# Revit family: Hager-Volta-IP30-Surface_mounted-leer-CH-de
name_source: partatom
category: Electrical Equipment
units: mm (PartAtom-declared; Revit-internal decimal feet)

## family parameters
Cut with Voids When Loaded = No
Host = Face
Panel Configuration = Two Columns, Circuits Across
Part Type = Panelboard
Room Calculation Point = No
Round Connector Dimension = Use Diameter
Shared = No

## types (1)
- Aufputz IP30 B305 H640 T96.5 12 Teilungseinheiten - VA48MD
    Default Elevation = 0 mm  [stored 0 ft]
    EF000003 - Montageart = EV000384 - Aufputz
    EF000008 - Breite = 305 mm  [stored 1.00066 ft]
    EF000040 - Höhe = 640 mm  [stored 2.09974 ft]
    EF000049 - Tiefe = 96 mm  [stored 0.314961 ft]
    EF000116 - RAL-Nummer = 9010
    EF000118 - Mit Montageplatte = Yes
    EF000218 - Einbautiefe = 0 mm  [stored 0 ft]
    EF000266 - Anzahl der Reihen = 0
    EF000332 - Einbauhöhe = 0 mm  [stored 0 ft]
    EF000339 - Art der Abdeckung = EV000494 - ohne
    EF000846 - Einbaubreite = 0 mm  [stored 0 ft]
    EF001062 - EMV-Ausführung = No
    EF001088 - Anbaumöglichkeit = Yes
    EF001131 - Innentiefe = 0 mm  [stored 0 ft]
    EF001134 - DIN-Schiene = No
    EF002950 - Breite in Teilungseinheiten = 12
    EF005474 - Schutzart (IP) = EV006410 - IP30
    EF006244 - Transparenter Deckel/Tür = No
    EF006306 - Mit Schloss = No
    EF009212 - Ausführung Deckel = EV009916 - mit Ausschnitt
    EF015776 - Erdungsklemmenblock = No
    EF015777 - Neutralleiterklemmenblock = No
    EF015941 - Signaldurchlassende Tür = No
    HG000001 - Anzahl der Spalten = 0
    HG000002 - Mit tür = No
    HG000003 - Bereich = Volta
    HG000004 - Herstellerreferenz = VA48MD
    HG000005 - Dicke = 3 mm  [stored 0.00984252 ft]
    HG000006 - Unterputz = No
    HG000007 - Anzahl der leeren Spalten = 0
    HG000008 - Anzahl der leeren Reihen = 0
    HG000009 - Doppelflügeligen Tür = No
    HG000010 - Asymmetrische Türen = No
    HG000011 - Leere Reihen von unten = No
    HG000017 - Distanz zwischen den Polen = 18 mm  [stored 0.0590551 ft]
    Manufacturer = Hager
    Model = VA48MD
    Type Comments = Volta

note: [stored X ft] marks values corroborated as IEEE doubles in the binary element streams (Revit-internal decimal feet)

## geometry (parser evidence)
native form markers: Sweep x16
no freeform markers — native parametric forms only
